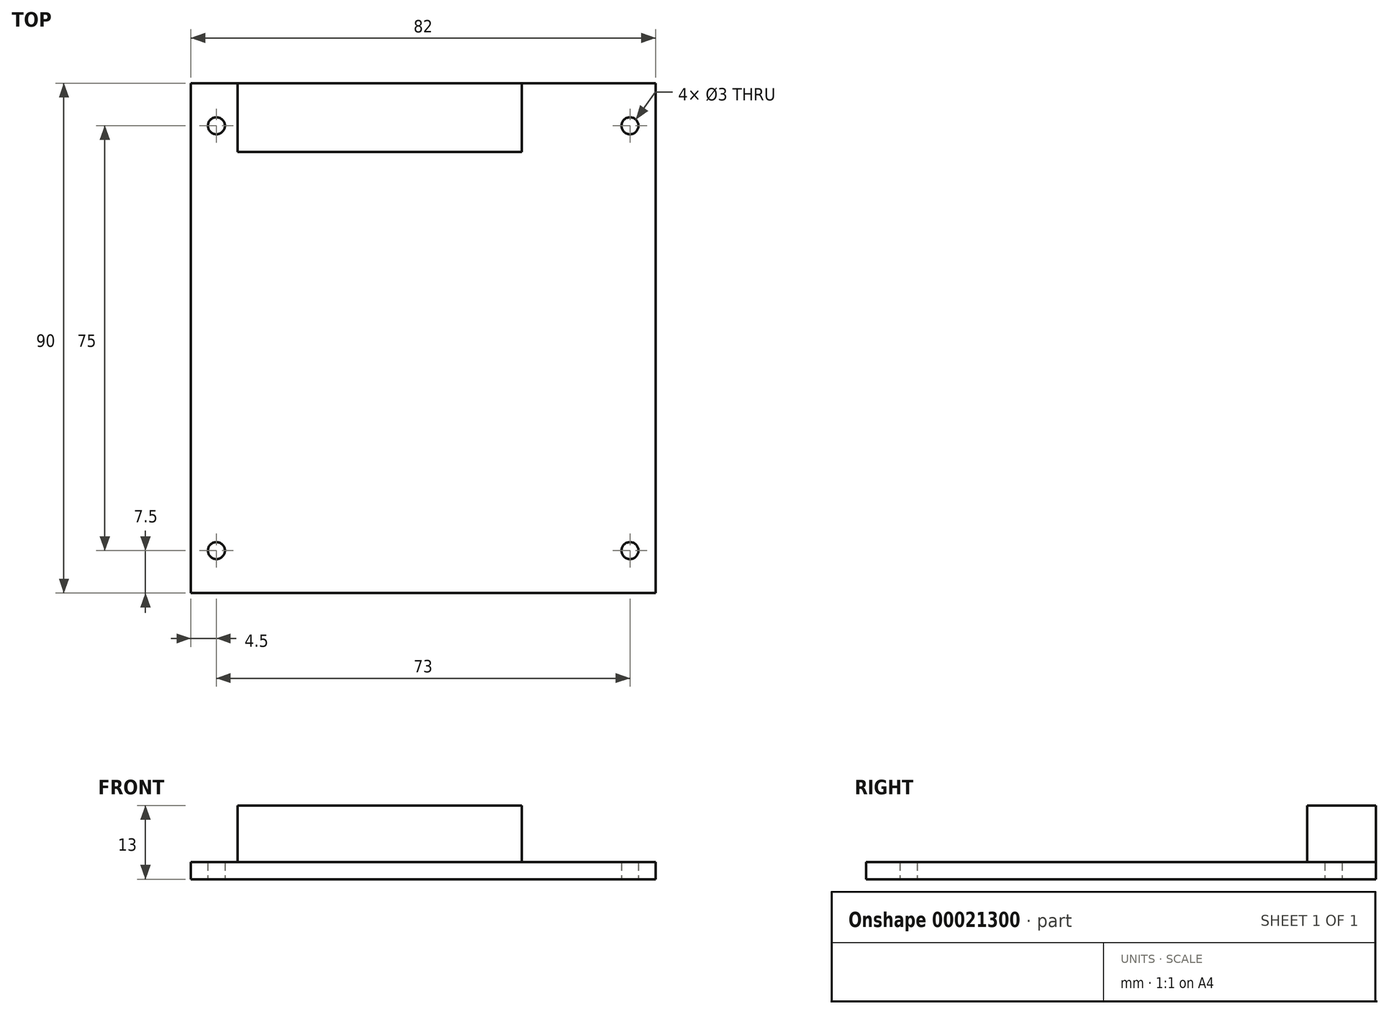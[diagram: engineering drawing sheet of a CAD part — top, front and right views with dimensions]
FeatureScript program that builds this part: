
annotation { "Feature Type Name" : "Feature", "Feature Type Description" : "" }
export const myFeature = defineFeature(function(context is Context, id is Id, definition is map)
    precondition{}
    {
        {
            var Q0;
            Q0=qCreatedBy(makeId("Top.planeOp"),FACE);
            var sketch = newSketch(context, id + "F0", { "sketchPlane" : qUnion([Q0])});
            skLineSegment(sketch, "E0.rect.bottom", {"start": v(41, 45) * mm, "end": v(-41, 45) * mm});
            skLineSegment(sketch, "E0.rect.top", {"start": v(41, -45) * mm, "end": v(-41, -45) * mm});
            skLineSegment(sketch, "E0.rect.left", {"start": v(41, 45) * mm, "end": v(41, -45) * mm});
            skLineSegment(sketch, "E0.rect.right", {"start": v(-41, 45) * mm, "end": v(-41, -45) * mm});
            skPoint(sketch, "E0.rect.middle", {"position": v(0, 0) * mm});
            skLineSegment(sketch, "E1.rect.bottom", {"start": v(36.5, 37.5) * mm, "end": v(-36.5, 37.5) * mm, "construction": true});
            skLineSegment(sketch, "E1.rect.top", {"start": v(36.5, -37.5) * mm, "end": v(-36.5, -37.5) * mm, "construction": true});
            skLineSegment(sketch, "E1.rect.left", {"start": v(36.5, 37.5) * mm, "end": v(36.5, -37.5) * mm, "construction": true});
            skLineSegment(sketch, "E1.rect.right", {"start": v(-36.5, 37.5) * mm, "end": v(-36.5, -37.5) * mm, "construction": true});
            skCircle(sketch, "E2", {"center": v(-36.5, 37.5) * mm, "radius": 1.5 * mm});
            skCircle(sketch, "E3", {"center": v(36.5, 37.5) * mm, "radius": 1.5 * mm});
            skCircle(sketch, "E4", {"center": v(36.5, -37.5) * mm, "radius": 1.5 * mm});
            skCircle(sketch, "E5", {"center": v(-36.5, -37.5) * mm, "radius": 1.5 * mm});
            skSolve(sketch);
        }
        {
            var Q0;
            Q0=makeQuery(id+"F0.imprint","IMPRINT",FACE,{"disambiguationData":[TD([[makeQuery(id+"F0.imprint","IMPRINT",EDGE,{"derivedFrom":sQuery(id+"F0.wireOp",EDGE,"E0.rect.bottom")}),1.0]])]});
            extrude(context, id + "F1", {"entities" : qUnion([Q0]), "depth" : 3 * mm});
        }
        {
            var Q0;
            Q0=makeQuery(id+"F1.opExtrude","CAP_FACE",FACE,{"disambiguationData":[OSD([sQuery(id+"F0.wireOp",EDGE,"E0.rect.bottom"),sQuery(id+"F0.wireOp",EDGE,"E0.rect.top"),sQuery(id+"F0.wireOp",EDGE,"E0.rect.left"),sQuery(id+"F0.wireOp",EDGE,"E0.rect.right"),sQuery(id+"F0.wireOp",EDGE,"E2"),sQuery(id+"F0.wireOp",EDGE,"E3"),sQuery(id+"F0.wireOp",EDGE,"E4"),sQuery(id+"F0.wireOp",EDGE,"E5")])],"isStart":false});
            var sketch = newSketch(context, id + "F2", { "sketchPlane" : qUnion([Q0])});
            skLineSegment(sketch, "E6.bottom", {"start": v(-32.79, 45) * mm, "end": v(17.43, 45) * mm});
            skLineSegment(sketch, "E6.top", {"start": v(-32.79, 32.9) * mm, "end": v(17.43, 32.9) * mm});
            skLineSegment(sketch, "E6.left", {"start": v(-32.79, 45) * mm, "end": v(-32.79, 32.9) * mm});
            skLineSegment(sketch, "E6.right", {"start": v(17.43, 45) * mm, "end": v(17.43, 32.9) * mm});
            skSolve(sketch);
        }
        {
            var Q0;
            Q0 = qSketchRegion(id + "F2", true);
            extrude(context, id + "F3", {"entities" : qUnion([Q0]), "operationType" : NewBodyOperationType.ADD, "depth" : 10 * mm});
        }
    });
